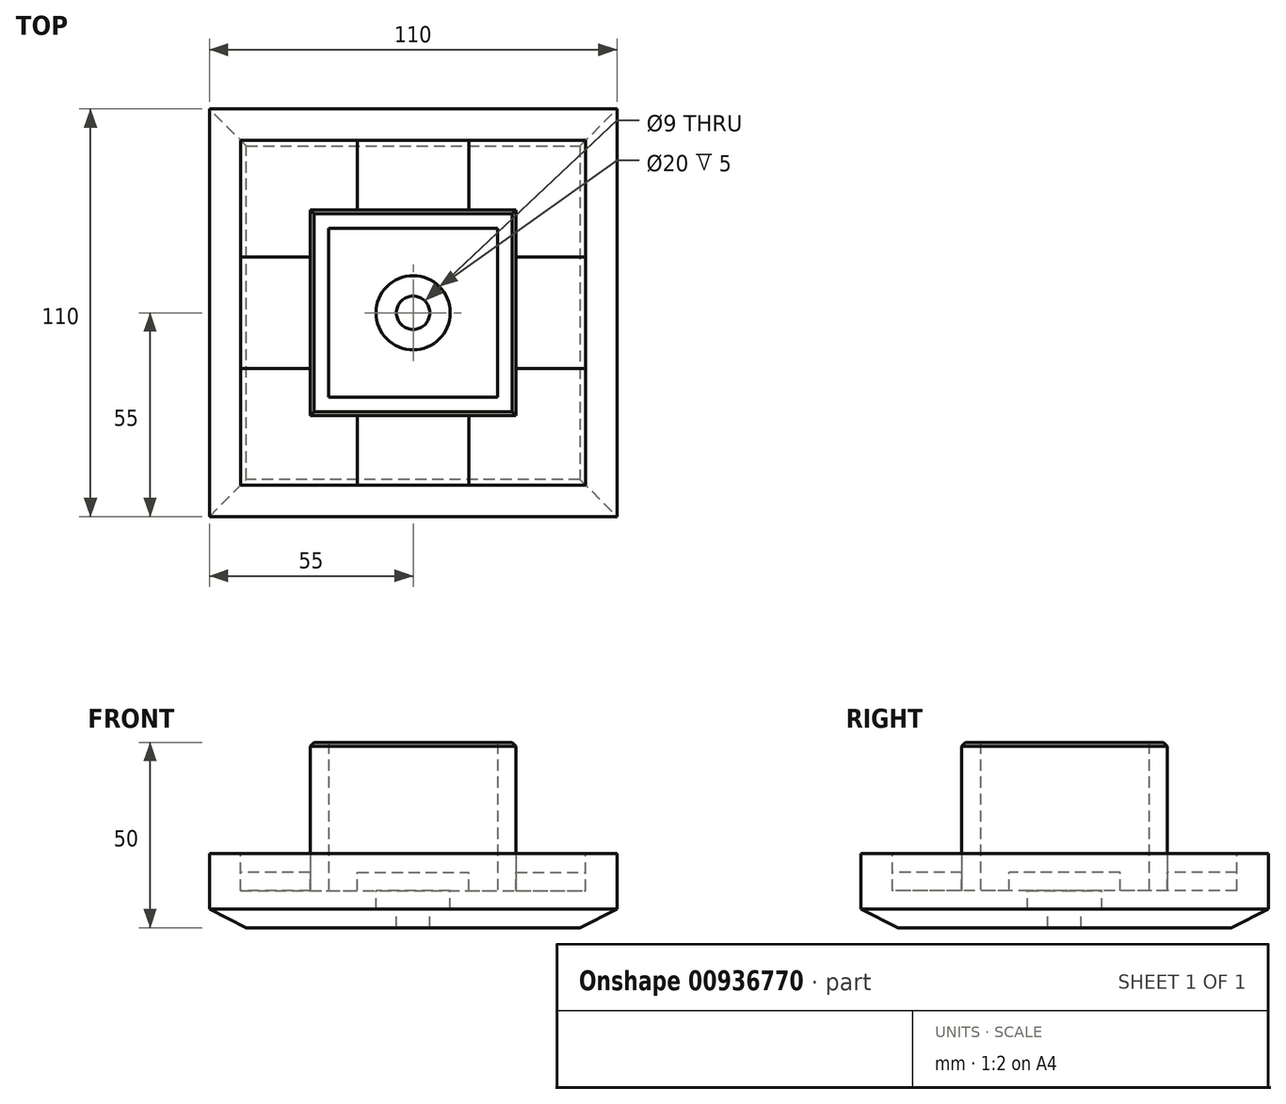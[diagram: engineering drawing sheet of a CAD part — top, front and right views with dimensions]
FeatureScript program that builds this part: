
annotation { "Feature Type Name" : "Feature", "Feature Type Description" : "" }
export const myFeature = defineFeature(function(context is Context, id is Id, definition is map)
    precondition{}
    {
        {
            var Q0;
            Q0=qCreatedBy(makeId("Top.planeOp"),FACE);
            var sketch = newSketch(context, id + "F0", { "sketchPlane" : qUnion([Q0])});
            skLineSegment(sketch, "E0.bottom", {"start": v(0, 0) * mm, "end": v(110, 0) * mm});
            skLineSegment(sketch, "E0.top", {"start": v(0, 110) * mm, "end": v(110, 110) * mm});
            skLineSegment(sketch, "E0.left", {"start": v(0, 0) * mm, "end": v(0, 110) * mm});
            skLineSegment(sketch, "E0.right", {"start": v(110, 0) * mm, "end": v(110, 110) * mm});
            skSolve(sketch);
        }
        {
            var Q0;
            Q0=makeQuery(id+"F0.imprint","IMPRINT",FACE,{"disambiguationData":[TD([[makeQuery(id+"F0.imprint","IMPRINT",EDGE,{"derivedFrom":sQuery(id+"F0.wireOp",EDGE,"E0.bottom")}),1.0]])]});
            extrude(context, id + "F1", {"entities" : qUnion([Q0]), "depth" : 20 * mm, "offsetDistance" : 25 * mm});
        }
        {
            var Q0;
            Q0=makeQuery(id+"F1.opExtrude","CAP_FACE",FACE,{"disambiguationData":[OSD([sQuery(id+"F0.wireOp",EDGE,"E0.bottom"),sQuery(id+"F0.wireOp",EDGE,"E0.top"),sQuery(id+"F0.wireOp",EDGE,"E0.left"),sQuery(id+"F0.wireOp",EDGE,"E0.right")])],"isStart":false});
            var sketch = newSketch(context, id + "F2", { "sketchPlane" : qUnion([Q0])});
            skLineSegment(sketch, "E1.bottom", {"start": v(0, 55) * mm, "end": v(110, 55) * mm, "construction": true});
            skLineSegment(sketch, "E1.top", {"start": v(0, 55) * mm, "end": v(110, 55) * mm, "construction": true});
            skLineSegment(sketch, "E1.left", {"start": v(0, 55) * mm, "end": v(0, 55) * mm});
            skLineSegment(sketch, "E1.right", {"start": v(110, 55) * mm, "end": v(110, 55) * mm});
            skLineSegment(sketch, "E2.bottom", {"start": v(55, 110) * mm, "end": v(55, 110) * mm});
            skLineSegment(sketch, "E2.top", {"start": v(55, 0) * mm, "end": v(55, 0) * mm});
            skLineSegment(sketch, "E2.left", {"start": v(55, 110) * mm, "end": v(55, 0) * mm, "construction": true});
            skLineSegment(sketch, "E2.right", {"start": v(55, 110) * mm, "end": v(55, 0) * mm, "construction": true});
            skLineSegment(sketch, "E3.bottom", {"start": v(27.25, 82.75) * mm, "end": v(82.75, 82.75) * mm});
            skLineSegment(sketch, "E3.top", {"start": v(27.25, 27.25) * mm, "end": v(82.75, 27.25) * mm});
            skLineSegment(sketch, "E3.left", {"start": v(27.25, 82.75) * mm, "end": v(27.25, 27.25) * mm});
            skLineSegment(sketch, "E3.right", {"start": v(82.75, 82.75) * mm, "end": v(82.75, 27.25) * mm});
            skPoint(sketch, "E3.middle", {"position": v(55, 55) * mm});
            skLineSegment(sketch, "E4.bottom", {"start": v(8.5, 101.5) * mm, "end": v(101.5, 101.5) * mm});
            skLineSegment(sketch, "E4.top", {"start": v(8.5, 8.5) * mm, "end": v(101.5, 8.5) * mm});
            skLineSegment(sketch, "E4.left", {"start": v(8.5, 101.5) * mm, "end": v(8.5, 8.5) * mm});
            skLineSegment(sketch, "E4.right", {"start": v(101.5, 101.5) * mm, "end": v(101.5, 8.5) * mm});
            skLineSegment(sketch, "E5.bottom", {"start": v(32.25, 77.75) * mm, "end": v(77.75, 77.75) * mm});
            skLineSegment(sketch, "E5.top", {"start": v(32.25, 32.25) * mm, "end": v(77.75, 32.25) * mm});
            skLineSegment(sketch, "E5.left", {"start": v(32.25, 77.75) * mm, "end": v(32.25, 32.25) * mm});
            skLineSegment(sketch, "E5.right", {"start": v(77.75, 77.75) * mm, "end": v(77.75, 32.25) * mm});
            skCircle(sketch, "E6", {"center": v(55, 55) * mm, "radius": 4.5 * mm});
            skLineSegment(sketch, "E7", {"start": v(40, 101.5) * mm, "end": v(40, 82.75) * mm});
            skLineSegment(sketch, "E8", {"start": v(27.25, 70) * mm, "end": v(8.5, 70) * mm});
            skLineSegment(sketch, "E9", {"start": v(8.5, 40) * mm, "end": v(27.25, 40) * mm});
            skLineSegment(sketch, "E10", {"start": v(40, 27.25) * mm, "end": v(40, 8.5) * mm});
            skLineSegment(sketch, "E11", {"start": v(70, 27.25) * mm, "end": v(70, 8.5) * mm});
            skLineSegment(sketch, "E12", {"start": v(82.75, 40) * mm, "end": v(101.5, 40) * mm});
            skLineSegment(sketch, "E13", {"start": v(82.75, 70) * mm, "end": v(101.5, 70) * mm});
            skLineSegment(sketch, "E14", {"start": v(70, 101.5) * mm, "end": v(70, 82.75) * mm});
            skCircle(sketch, "E15", {"center": v(55, 55) * mm, "radius": 10 * mm});
            skSolve(sketch);
        }
        {
            var Q0;
            Q0=makeQuery(id+"F2.imprint","IMPRINT",FACE,{"disambiguationData":[TD([[makeQuery(id+"F2.imprint","IMPRINT",EDGE,{"derivedFrom":sQuery(id+"F2.wireOp",EDGE,"E3.bottom")}),1.0]])]});
            var Q1;
            {var subQ0=sQuery(id+"F2.wireOp",EDGE,"E12");Q1=makeQuery(id+"F2.imprint","IMPRINT",FACE,{"disambiguationData":[TD([[makeQuery(id+"F2.imprint","IMPRINT",EDGE,{"derivedFrom":subQ0}),1.0]])]});}
            var Q2;
            {var subQ0=sQuery(id+"F2.wireOp",EDGE,"E10");Q2=makeQuery(id+"F2.imprint","IMPRINT",FACE,{"disambiguationData":[TD([[makeQuery(id+"F2.imprint","IMPRINT",EDGE,{"derivedFrom":subQ0}),1.0]])]});}
            var Q3;
            {var subQ0=sQuery(id+"F2.wireOp",EDGE,"E8");Q3=makeQuery(id+"F2.imprint","IMPRINT",FACE,{"disambiguationData":[TD([[makeQuery(id+"F2.imprint","IMPRINT",EDGE,{"derivedFrom":subQ0}),1.0]])]});}
            extrude(context, id + "F3", {"entities" : qUnion([Q0, Q1, Q2, Q3]), "operationType" : NewBodyOperationType.REMOVE, "oppositeDirection" : true, "depth" : 5 * mm, "offsetDistance" : 25 * mm});
        }
        {
            var Q0;
            Q0=makeQuery(id+"F2.imprint","IMPRINT",FACE,{"disambiguationData":[TD([[makeQuery(id+"F2.imprint","IMPRINT",EDGE,{"derivedFrom":sQuery(id+"F2.wireOp",EDGE,"E3.bottom")}),-1.0]])]});
            extrude(context, id + "F4", {"entities" : qUnion([Q0]), "operationType" : NewBodyOperationType.ADD, "depth" : 30 * mm, "offsetDistance" : 25 * mm});
        }
        {
            var Q0;
            Q0=makeQuery(id+"F2.imprint","IMPRINT",FACE,{"disambiguationData":[TD([[makeQuery(id+"F2.imprint","IMPRINT",EDGE,{"derivedFrom":sQuery(id+"F2.wireOp",EDGE,"E6")}),1.0]])]});
            extrude(context, id + "F5", {"entities" : qUnion([Q0]), "operationType" : NewBodyOperationType.REMOVE, "endBound" : BoundingType.THROUGH_ALL, "oppositeDirection" : true, "depth" : 25 * mm, "offsetDistance" : 25 * mm});
        }
        {
            var Q0;
            Q0=makeQuery(id+"F2.imprint","IMPRINT",FACE,{"disambiguationData":[TD([[makeQuery(id+"F2.imprint","IMPRINT",EDGE,{"derivedFrom":sQuery(id+"F2.wireOp",EDGE,"E5.bottom")}),-1.0]])]});
            extrude(context, id + "F6", {"entities" : qUnion([Q0]), "operationType" : NewBodyOperationType.REMOVE, "oppositeDirection" : true, "depth" : 10 * mm, "offsetDistance" : 25 * mm});
        }
        {
            var Q0;
            Q0=makeQuery(id+"F1.opExtrude","CAP_EDGE",EDGE,{"disambiguationData":[OSD([sQuery(id+"F0.wireOp",EDGE,"E0.top")])],"isStart":true});
            var Q1;
            Q1=makeQuery(id+"F1.opExtrude","CAP_EDGE",EDGE,{"disambiguationData":[OSD([sQuery(id+"F0.wireOp",EDGE,"E0.left")])],"isStart":true});
            var Q2;
            Q2=makeQuery(id+"F1.opExtrude","CAP_EDGE",EDGE,{"disambiguationData":[OSD([sQuery(id+"F0.wireOp",EDGE,"E0.bottom")])],"isStart":true});
            var Q3;
            Q3=makeQuery(id+"F1.opExtrude","CAP_EDGE",EDGE,{"disambiguationData":[OSD([sQuery(id+"F0.wireOp",EDGE,"E0.right")])],"isStart":true});
            chamfer(context, id + "F7", {"entities" : qUnion([Q0, Q1, Q2, Q3]), "chamferType" : ChamferType.TWO_OFFSETS, "width1" : 10 * mm, "oppositeDirection" : false, "width2" : 5 * mm, "tangentPropagation" : true});
        }
        {
            var Q0;
            Q0=makeQuery(id+"F4.opExtrude","CAP_EDGE",EDGE,{"disambiguationData":[OSD([sQuery(id+"F2.wireOp",EDGE,"E3.top")])],"isStart":false});
            var Q1;
            Q1=makeQuery(id+"F4.opExtrude","CAP_EDGE",EDGE,{"disambiguationData":[OSD([sQuery(id+"F2.wireOp",EDGE,"E3.left")])],"isStart":false});
            var Q2;
            Q2=makeQuery(id+"F4.opExtrude","CAP_EDGE",EDGE,{"disambiguationData":[OSD([sQuery(id+"F2.wireOp",EDGE,"E3.right")])],"isStart":false});
            var Q3;
            Q3=makeQuery(id+"F4.opExtrude","CAP_EDGE",EDGE,{"disambiguationData":[OSD([sQuery(id+"F2.wireOp",EDGE,"E3.bottom")])],"isStart":false});
            chamfer(context, id + "F8", {"entities" : qUnion([Q0, Q1, Q2, Q3]), "width" : 1 * mm, "tangentPropagation" : true});
        }
        {
            var Q0;
            {var subQ4=sQuery(id+"F2.wireOp",EDGE,"E7");Q0=makeQuery(id+"F2.imprint","IMPRINT",FACE,{"disambiguationData":[TD([[makeQuery(id+"F2.imprint","IMPRINT",EDGE,{"derivedFrom":subQ4}),-1.0]])]});}
            var Q1;
            {var subQ3=sQuery(id+"F2.wireOp",EDGE,"E9");Q1=makeQuery(id+"F2.imprint","IMPRINT",FACE,{"disambiguationData":[TD([[makeQuery(id+"F2.imprint","IMPRINT",EDGE,{"derivedFrom":subQ3}),-1.0]])]});}
            var Q2;
            {var subQ4=sQuery(id+"F2.wireOp",EDGE,"E11");Q2=makeQuery(id+"F2.imprint","IMPRINT",FACE,{"disambiguationData":[TD([[makeQuery(id+"F2.imprint","IMPRINT",EDGE,{"derivedFrom":subQ4}),1.0]])]});}
            var Q3;
            {var subQ3=sQuery(id+"F2.wireOp",EDGE,"E13");Q3=makeQuery(id+"F2.imprint","IMPRINT",FACE,{"disambiguationData":[TD([[makeQuery(id+"F2.imprint","IMPRINT",EDGE,{"derivedFrom":subQ3}),1.0]])]});}
            extrude(context, id + "F9", {"entities" : qUnion([Q0, Q1, Q2, Q3]), "operationType" : NewBodyOperationType.REMOVE, "oppositeDirection" : true, "depth" : 10 * mm, "offsetDistance" : 25 * mm});
        }
        {
            var Q0;
            Q0=makeQuery(id+"F2.imprint","IMPRINT",FACE,{"disambiguationData":[TD([[makeQuery(id+"F2.imprint","IMPRINT",EDGE,{"derivedFrom":sQuery(id+"F2.wireOp",EDGE,"E6")}),-1.0]])]});
            extrude(context, id + "F10", {"entities" : qUnion([Q0]), "operationType" : NewBodyOperationType.REMOVE, "oppositeDirection" : true, "depth" : 15 * mm, "offsetDistance" : 25 * mm});
        }
    });
